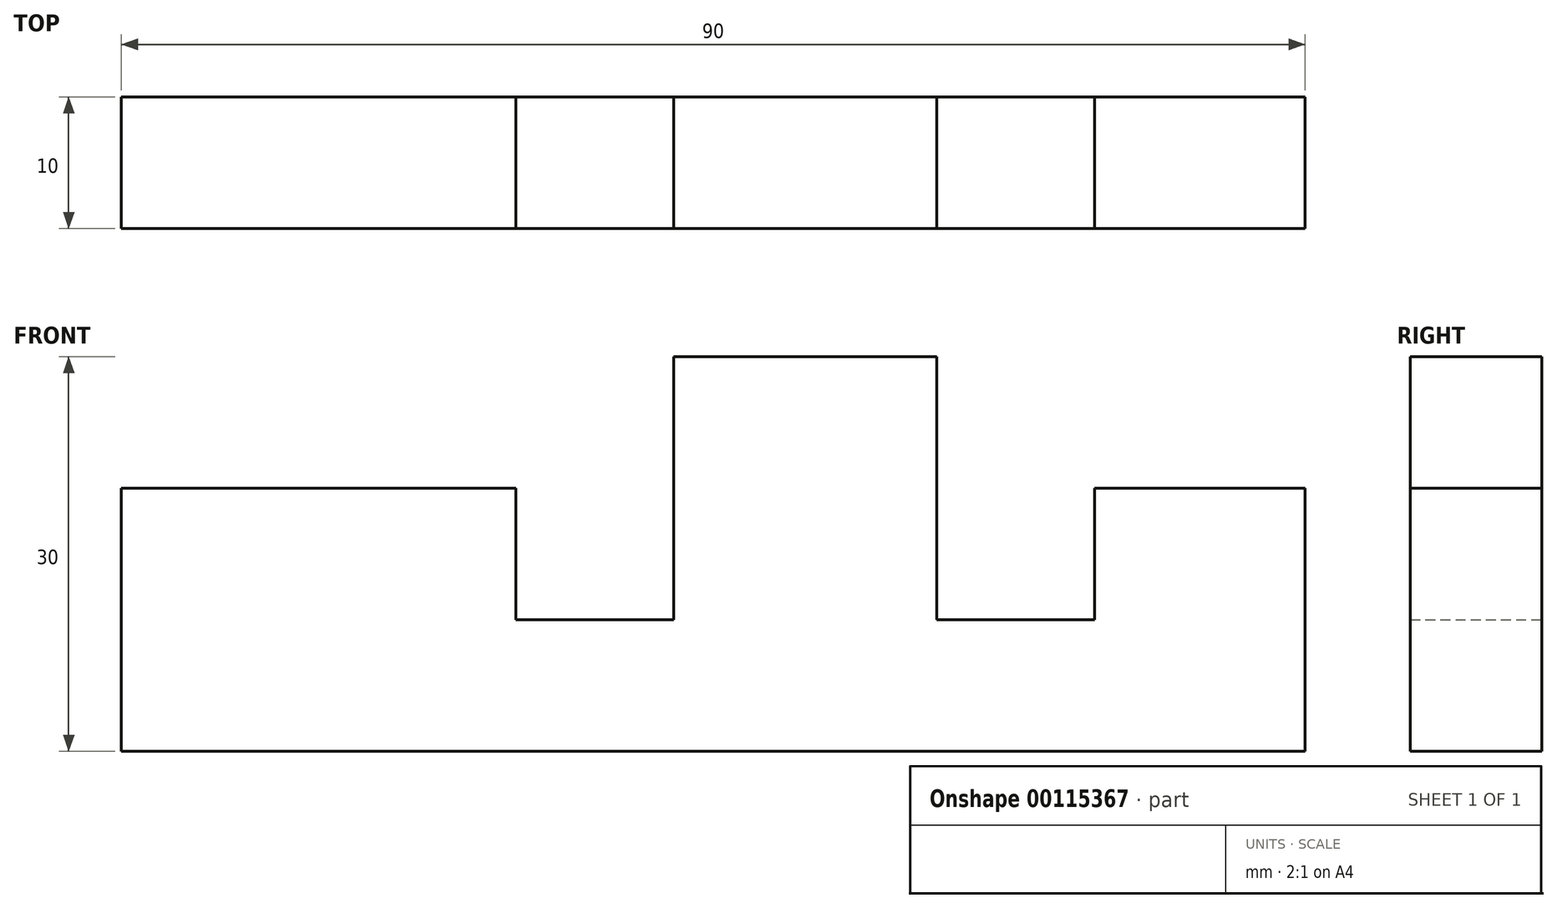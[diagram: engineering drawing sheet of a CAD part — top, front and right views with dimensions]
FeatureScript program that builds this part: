
annotation { "Feature Type Name" : "Feature", "Feature Type Description" : "" }
export const myFeature = defineFeature(function(context is Context, id is Id, definition is map)
    precondition{}
    {
        {
            var Q0;
            Q0=qCreatedBy(makeId("Front.planeOp"),FACE);
            var sketch = newSketch(context, id + "F0", { "sketchPlane" : qUnion([Q0])});
            skLineSegment(sketch, "E0", {"start": v(0, 20) * mm, "end": v(0, 0) * mm});
            skLineSegment(sketch, "E1", {"start": v(0, 0) * mm, "end": v(90, 0) * mm});
            skLineSegment(sketch, "E2", {"start": v(90, 0) * mm, "end": v(90, 20) * mm});
            skLineSegment(sketch, "E3", {"start": v(90, 20) * mm, "end": v(74, 20) * mm});
            skLineSegment(sketch, "E4", {"start": v(74, 20) * mm, "end": v(74, 10) * mm});
            skLineSegment(sketch, "E5", {"start": v(74, 10) * mm, "end": v(62, 10) * mm});
            skLineSegment(sketch, "E6", {"start": v(62, 10) * mm, "end": v(62, 30) * mm});
            skLineSegment(sketch, "E7", {"start": v(62, 30) * mm, "end": v(42, 30) * mm});
            skLineSegment(sketch, "E8", {"start": v(42, 30) * mm, "end": v(42, 10) * mm});
            skLineSegment(sketch, "E9", {"start": v(42, 10) * mm, "end": v(30, 10) * mm});
            skLineSegment(sketch, "E10", {"start": v(30, 10) * mm, "end": v(30, 20) * mm});
            skLineSegment(sketch, "E11", {"start": v(30, 20) * mm, "end": v(0, 20) * mm});
            skLineSegment(sketch, "E12", {"start": v(0, 20) * mm, "end": v(123.07, 20) * mm, "construction": true});
            skSolve(sketch);
        }
        {
            var Q0;
            Q0=makeQuery(id+"F0.imprint","IMPRINT",FACE,{"disambiguationData":[TD([[makeQuery(id+"F0.imprint","IMPRINT",EDGE,{"derivedFrom":sQuery(id+"F0.wireOp",EDGE,"E0")}),1.0]])]});
            extrude(context, id + "F1", {"entities" : qUnion([Q0]), "depth" : 10 * mm});
        }
    });
